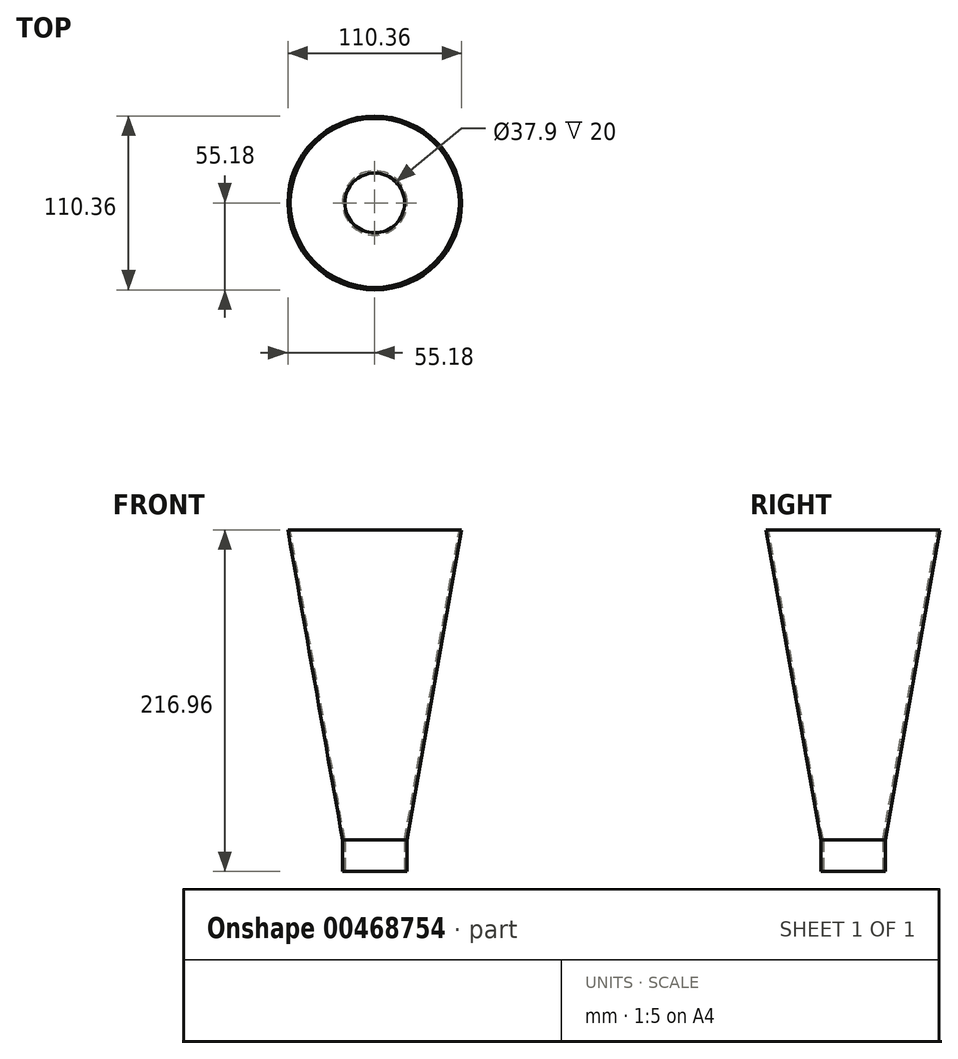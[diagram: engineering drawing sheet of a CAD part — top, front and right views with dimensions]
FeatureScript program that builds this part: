
annotation { "Feature Type Name" : "Feature", "Feature Type Description" : "" }
export const myFeature = defineFeature(function(context is Context, id is Id, definition is map)
    precondition{}
    {
        {
            var Q0;
            Q0=qCreatedBy(makeId("Front.planeOp"),FACE);
            var sketch = newSketch(context, id + "F0", { "sketchPlane" : qUnion([Q0])});
            skLineSegment(sketch, "E0", {"start": v(0, -36.23) * mm, "end": v(0, 116.39) * mm, "construction": true});
            skLineSegment(sketch, "E1", {"start": v(-20.45, 0) * mm, "end": v(-20.45, 20) * mm});
            skLineSegment(sketch, "E2", {"start": v(-20.45, 20) * mm, "end": v(-55.18, 216.96) * mm});
            skLineSegment(sketch, "E3", {"start": v(-20.45, 0) * mm, "end": v(-18.95, 0) * mm});
            skLineSegment(sketch, "E4", {"start": v(-18.95, 0) * mm, "end": v(-18.95, 20) * mm});
            skLineSegment(sketch, "E5", {"start": v(-18.95, 20) * mm, "end": v(-53.68, 216.96) * mm});
            skLineSegment(sketch, "E6", {"start": v(-53.68, 216.96) * mm, "end": v(-55.18, 216.96) * mm});
            skSolve(sketch);
        }
        {
            var Q0;
            Q0=makeQuery(id+"F0.imprint","IMPRINT",FACE,{"disambiguationData":[TD([[makeQuery(id+"F0.imprint","IMPRINT",EDGE,{"derivedFrom":sQuery(id+"F0.wireOp",EDGE,"E1")}),-1.0]])]});
            var Q1;
            Q1=sQuery(id+"F0.wireOp",EDGE,"E0");
            revolve(context, id + "F1", {"entities" : qUnion([Q0]), "axis" : qUnion([Q1]), "revolveType" : RevolveType.FULL});
        }
    });
